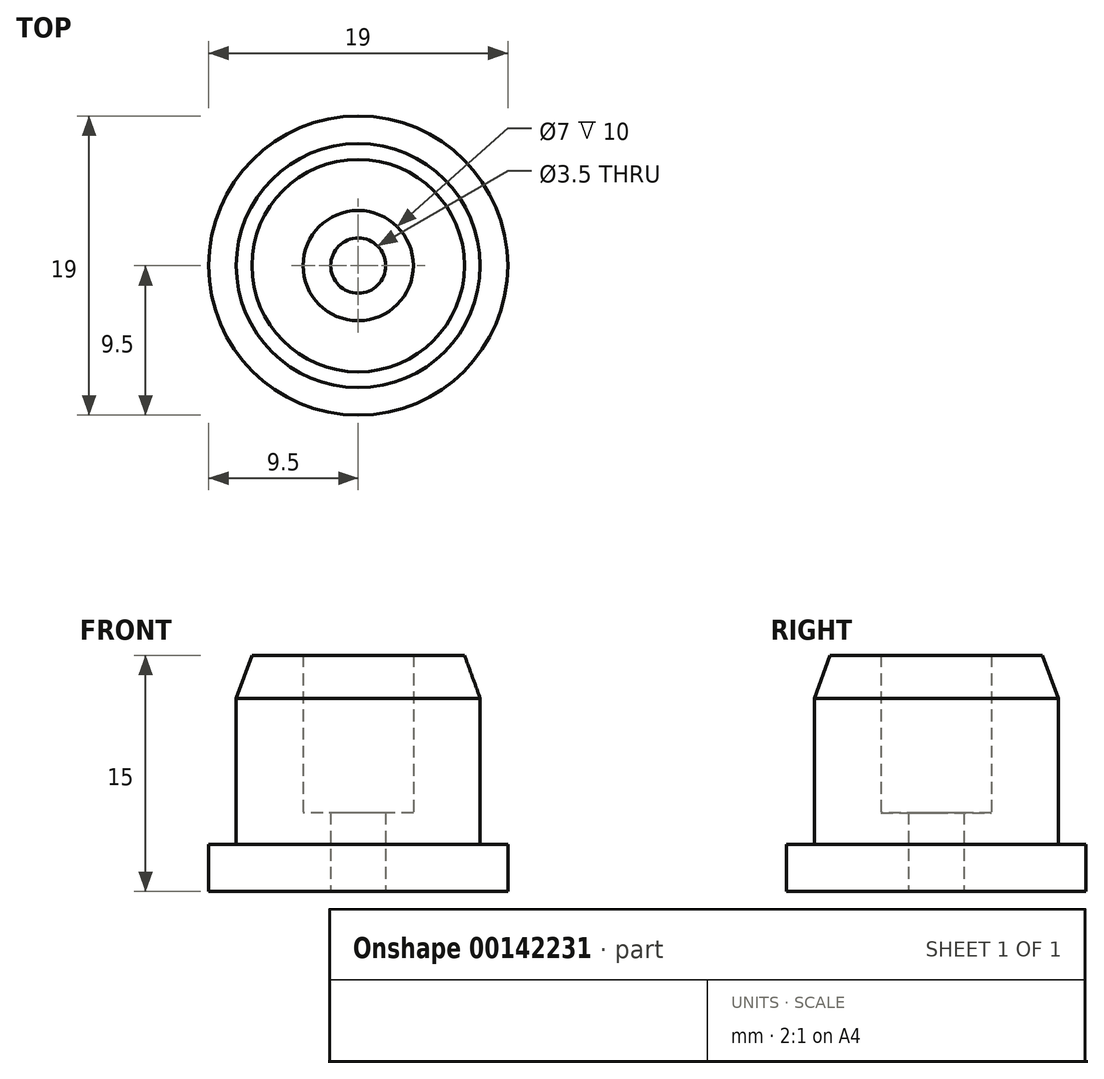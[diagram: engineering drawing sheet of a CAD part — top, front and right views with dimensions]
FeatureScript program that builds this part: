
annotation { "Feature Type Name" : "Feature", "Feature Type Description" : "" }
export const myFeature = defineFeature(function(context is Context, id is Id, definition is map)
    precondition{}
    {
        {
            var Q0;
            Q0=qCreatedBy(makeId("Top.planeOp"),FACE);
            var sketch = newSketch(context, id + "F0", { "sketchPlane" : qUnion([Q0])});
            skCircle(sketch, "E0", {"center": v(0, 0) * mm, "radius": 9.5 * mm});
            skCircle(sketch, "E1", {"center": v(0, 0) * mm, "radius": 7.75 * mm});
            skCircle(sketch, "E2", {"center": v(0, 0) * mm, "radius": 1.75 * mm});
            skCircle(sketch, "E3", {"center": v(0, 0) * mm, "radius": 3.5 * mm});
            skSolve(sketch);
        }
        {
            var Q0;
            Q0=makeQuery(id+"F0.imprint","IMPRINT",FACE,{"disambiguationData":[TD([[makeQuery(id+"F0.imprint","IMPRINT",EDGE,{"derivedFrom":sQuery(id+"F0.wireOp",EDGE,"E0")}),1.0]])]});
            extrude(context, id + "F1", {"entities" : qUnion([Q0]), "depth" : 3 * mm});
        }
        {
            var Q0;
            Q0=makeQuery(id+"F0.imprint","IMPRINT",FACE,{"disambiguationData":[TD([[makeQuery(id+"F0.imprint","IMPRINT",EDGE,{"derivedFrom":sQuery(id+"F0.wireOp",EDGE,"E1")}),1.0]])]});
            extrude(context, id + "F2", {"entities" : qUnion([Q0]), "operationType" : NewBodyOperationType.ADD, "depth" : 15 * mm});
        }
        {
            var Q0;
            Q0=makeQuery(id+"F0.imprint","IMPRINT",FACE,{"disambiguationData":[TD([[makeQuery(id+"F0.imprint","IMPRINT",EDGE,{"derivedFrom":sQuery(id+"F0.wireOp",EDGE,"E2")}),-1.0]])]});
            extrude(context, id + "F3", {"entities" : qUnion([Q0]), "operationType" : NewBodyOperationType.ADD, "depth" : 5 * mm});
        }
        {
            var Q0;
            Q0=makeQuery(id+"F2.opExtrude","CAP_EDGE",EDGE,{"disambiguationData":[OSD([sQuery(id+"F0.wireOp",EDGE,"E1")])],"isStart":false});
            chamfer(context, id + "F4", {"entities" : qUnion([Q0]), "chamferType" : ChamferType.OFFSET_ANGLE, "width" : 1 * mm, "oppositeDirection" : false, "angle" : 70 * degree, "tangentPropagation" : true});
        }
    });
